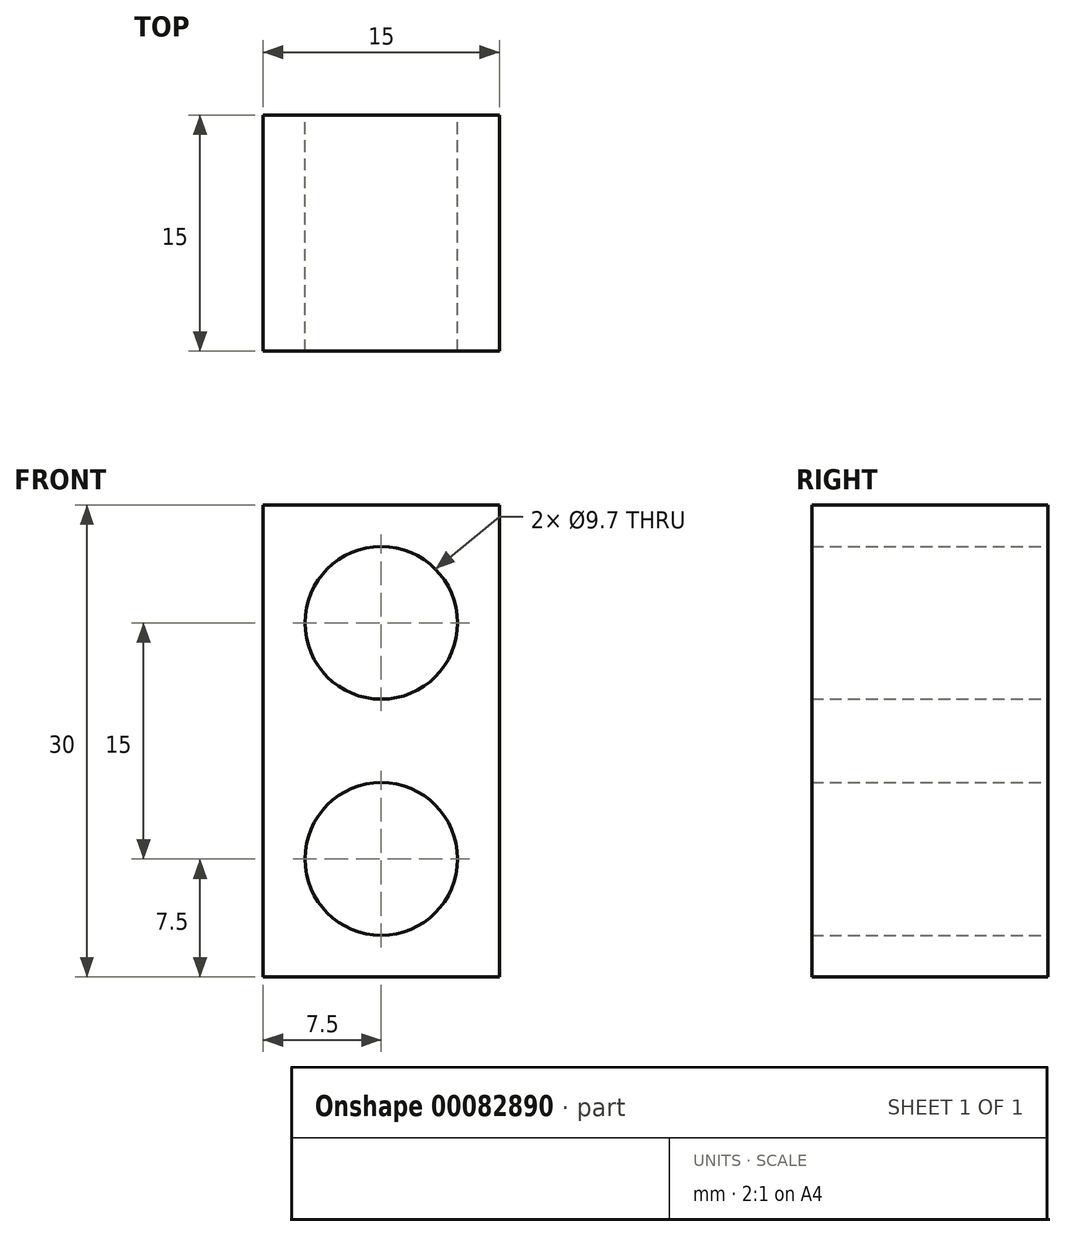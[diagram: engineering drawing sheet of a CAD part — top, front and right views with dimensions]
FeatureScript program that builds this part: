
annotation { "Feature Type Name" : "Feature", "Feature Type Description" : "" }
export const myFeature = defineFeature(function(context is Context, id is Id, definition is map)
    precondition{}
    {
        {
            var Q0;
            Q0=qCreatedBy(makeId("Front.planeOp"),FACE);
            var sketch = newSketch(context, id + "F0", { "sketchPlane" : qUnion([Q0])});
            skLineSegment(sketch, "E0.bottom", {"start": v(-7.5, 15) * mm, "end": v(7.5, 15) * mm});
            skLineSegment(sketch, "E0.top", {"start": v(-7.5, -15) * mm, "end": v(7.5, -15) * mm});
            skLineSegment(sketch, "E0.left", {"start": v(-7.5, 15) * mm, "end": v(-7.5, -15) * mm});
            skLineSegment(sketch, "E0.right", {"start": v(7.5, 15) * mm, "end": v(7.5, -15) * mm});
            skPoint(sketch, "E0.middle", {"position": v(0, 0) * mm});
            skCircle(sketch, "E1", {"center": v(0, 7.5) * mm, "radius": 4.85 * mm});
            skPoint(sketch, "E1.centerSnap0", {"position": v(0, 15) * mm});
            skCircle(sketch, "E2", {"center": v(0, -7.5) * mm, "radius": 4.85 * mm});
            skLineSegment(sketch, "E3", {"start": v(0, 0) * mm, "end": v(0, 15) * mm, "construction": true});
            skLineSegment(sketch, "E4", {"start": v(0, 0) * mm, "end": v(0, -15) * mm, "construction": true});
            skSolve(sketch);
        }
        {
            var Q0;
            Q0=makeQuery(id+"F0.imprint","IMPRINT",FACE,{"disambiguationData":[TD([[makeQuery(id+"F0.imprint","IMPRINT",EDGE,{"derivedFrom":sQuery(id+"F0.wireOp",EDGE,"E0.bottom")}),-1.0]])]});
            extrude(context, id + "F1", {"entities" : qUnion([Q0]), "endBound" : BoundingType.SYMMETRIC, "depth" : 15 * mm});
        }
    });
